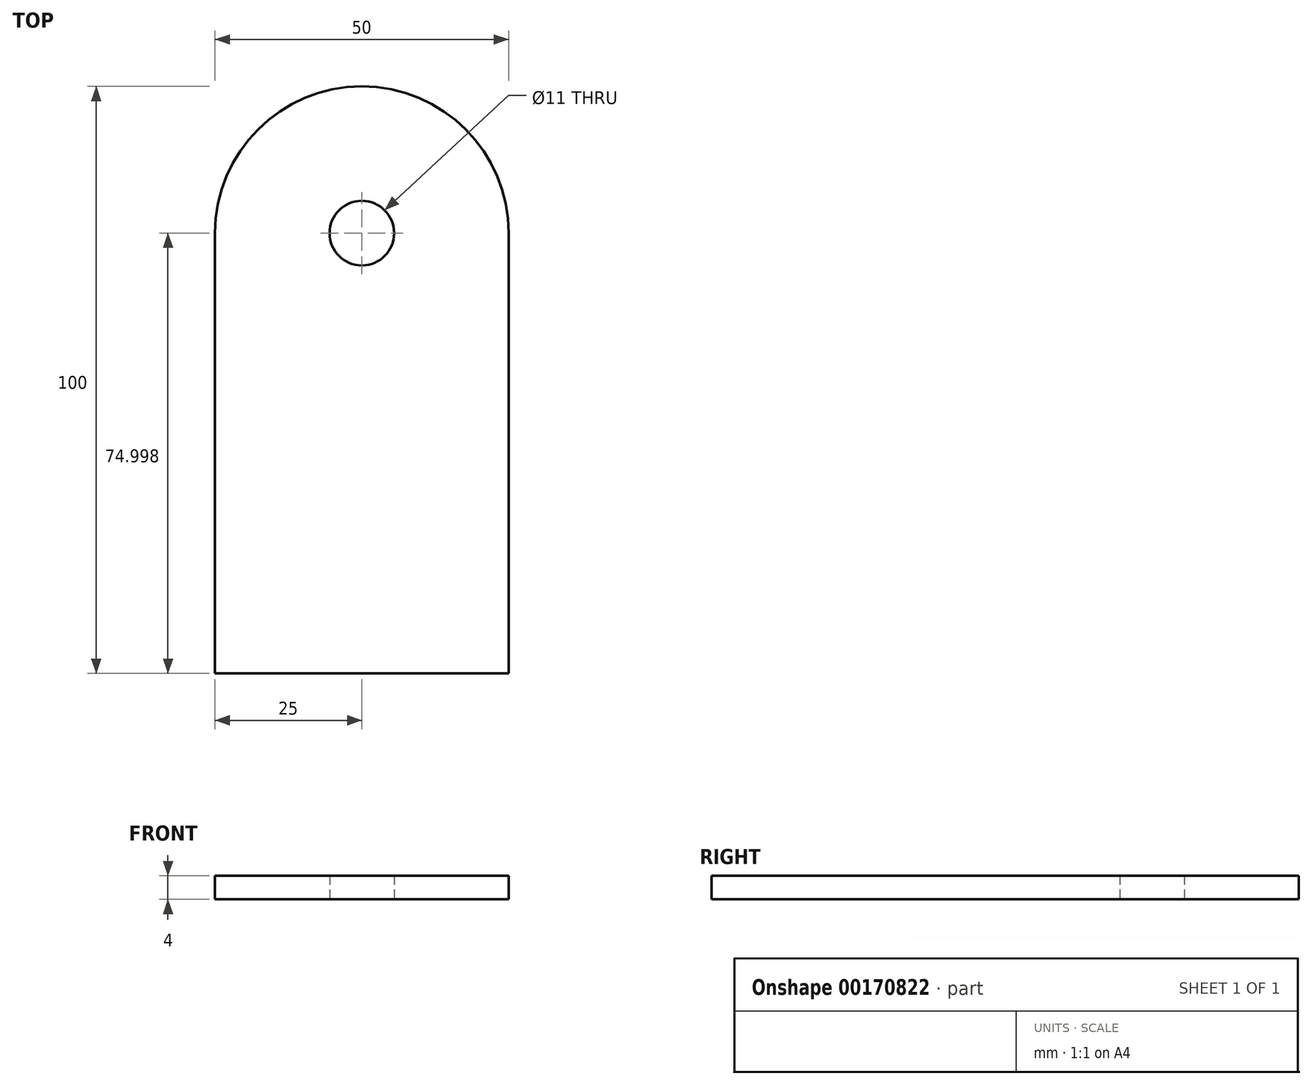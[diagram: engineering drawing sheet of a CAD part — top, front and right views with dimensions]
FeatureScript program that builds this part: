
annotation { "Feature Type Name" : "Feature", "Feature Type Description" : "" }
export const myFeature = defineFeature(function(context is Context, id is Id, definition is map)
    precondition{}
    {
        {
            var Q0;
            Q0=qCreatedBy(makeId("Top.planeOp"),FACE);
            var sketch = newSketch(context, id + "F0", { "sketchPlane" : qUnion([Q0])});
            skLineSegment(sketch, "E0.bottom", {"start": v(22.83, 46.74) * mm, "end": v(-27.17, 46.74) * mm});
            skLineSegment(sketch, "E0.top", {"start": v(22.83, -28.26) * mm, "end": v(-27.17, -28.26) * mm});
            skLineSegment(sketch, "E0.left", {"start": v(22.83, 46.74) * mm, "end": v(22.83, -28.26) * mm});
            skLineSegment(sketch, "E0.right", {"start": v(-27.17, 46.74) * mm, "end": v(-27.17, -28.26) * mm});
            skArc(sketch, "E1", {"start": v(22.83, 46.74) * mm, "mid": v(-2.17, 71.74) * mm, "end": v(-27.17, 46.74) * mm});
            skCircle(sketch, "E2", {"center": v(-2.17, 46.74) * mm, "radius": 5.5 * mm});
            skPoint(sketch, "E3", {"position": v(-2.17, 71.74) * mm});
            skSolve(sketch);
        }
        {
            var Q0;
            Q0 = qSketchRegion(id + "F0", true);
            extrude(context, id + "F1", {"entities" : qUnion([Q0]), "depth" : 4 * mm});
        }
    });
